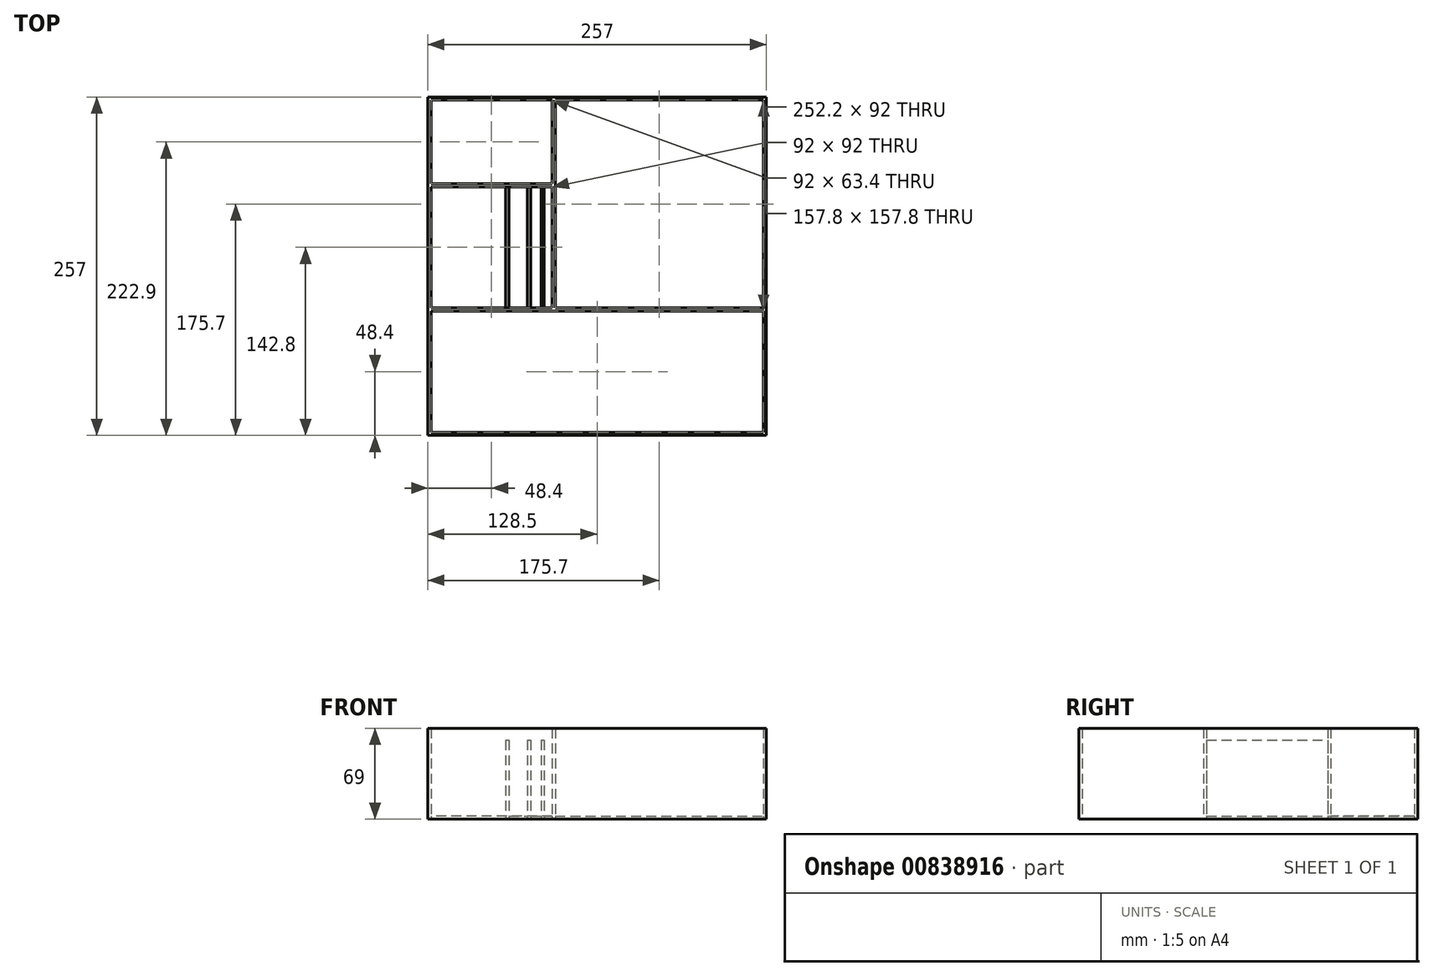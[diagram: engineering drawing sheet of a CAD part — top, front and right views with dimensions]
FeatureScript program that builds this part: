
annotation { "Feature Type Name" : "Feature", "Feature Type Description" : "" }
export const myFeature = defineFeature(function(context is Context, id is Id, definition is map)
    precondition{}
    {
        {
            var Q0;
            Q0=qCreatedBy(makeId("Top.planeOp"),FACE);
            var sketch = newSketch(context, id + "F0", { "sketchPlane" : qUnion([Q0])});
            skLineSegment(sketch, "E0.bottom", {"start": v(128.5, 128.5) * mm, "end": v(-128.5, 128.5) * mm});
            skLineSegment(sketch, "E0.top", {"start": v(128.5, -128.5) * mm, "end": v(-128.5, -128.5) * mm});
            skLineSegment(sketch, "E0.left", {"start": v(128.5, 128.5) * mm, "end": v(128.5, -128.5) * mm});
            skLineSegment(sketch, "E0.right", {"start": v(-128.5, 128.5) * mm, "end": v(-128.5, -128.5) * mm});
            skPoint(sketch, "E0.middle", {"position": v(0, 0) * mm});
            skLineSegment(sketch, "E1.0", {"start": v(-126.1, 126.1) * mm, "end": v(-126.1, -126.1) * mm});
            skLineSegment(sketch, "E1.1", {"start": v(126.1, 126.1) * mm, "end": v(-126.1, 126.1) * mm});
            skLineSegment(sketch, "E1.2", {"start": v(126.1, 126.1) * mm, "end": v(126.1, -126.1) * mm});
            skLineSegment(sketch, "E1.3", {"start": v(126.1, -126.1) * mm, "end": v(-126.1, -126.1) * mm});
            skLineSegment(sketch, "E2.bottom", {"start": v(-126.1, -126.1) * mm, "end": v(126.1, -126.1) * mm});
            skLineSegment(sketch, "E2.top", {"start": v(-126.1, -34.1) * mm, "end": v(126.1, -34.1) * mm});
            skLineSegment(sketch, "E2.left", {"start": v(-126.1, -126.1) * mm, "end": v(-126.1, -34.1) * mm});
            skLineSegment(sketch, "E2.right", {"start": v(126.1, -126.1) * mm, "end": v(126.1, -34.1) * mm});
            skLineSegment(sketch, "E3.0", {"start": v(-126.1, -31.7) * mm, "end": v(126.1, -31.7) * mm});
            skLineSegment(sketch, "E4.bottom", {"start": v(-126.1, -31.7) * mm, "end": v(-34.1, -31.7) * mm});
            skLineSegment(sketch, "E4.top", {"start": v(-126.1, 60.3) * mm, "end": v(-34.1, 60.3) * mm});
            skLineSegment(sketch, "E4.left", {"start": v(-126.1, -31.7) * mm, "end": v(-126.1, 60.3) * mm});
            skLineSegment(sketch, "E4.right", {"start": v(-34.1, -31.7) * mm, "end": v(-34.1, 60.3) * mm});
            skLineSegment(sketch, "E5", {"start": v(-34.1, 60.3) * mm, "end": v(-34.1, 126.1) * mm});
            skLineSegment(sketch, "E6.0", {"start": v(-126.1, 62.7) * mm, "end": v(-34.1, 62.7) * mm});
            skLineSegment(sketch, "E7.0", {"start": v(-31.7, 60.3) * mm, "end": v(-31.7, 126.1) * mm});
            skLineSegment(sketch, "E7.1", {"start": v(-31.7, -31.7) * mm, "end": v(-31.7, 60.3) * mm});
            skLineSegment(sketch, "E8.0", {"start": v(-40.1, -31.7) * mm, "end": v(-40.1, 60.3) * mm});
            skLineSegment(sketch, "E9.0", {"start": v(-42.5, -31.7) * mm, "end": v(-42.5, 60.3) * mm});
            skLineSegment(sketch, "E10.0", {"start": v(-50.5, -31.7) * mm, "end": v(-50.5, 60.3) * mm});
            skLineSegment(sketch, "E11.0", {"start": v(-52.9, -31.7) * mm, "end": v(-52.9, 60.3) * mm});
            skLineSegment(sketch, "E12.0", {"start": v(-66.9, -31.7) * mm, "end": v(-66.9, 60.3) * mm});
            skLineSegment(sketch, "E13.0", {"start": v(-69.3, -31.7) * mm, "end": v(-69.3, 60.3) * mm});
            skSolve(sketch);
        }
        {
            var Q0;
            {var subQ3=sQuery(id+"F0.wireOp",EDGE,"E6.0");Q0=makeQuery(id+"F0.imprint","IMPRINT",FACE,{"disambiguationData":[TD([[makeQuery(id+"F0.imprint","IMPRINT",EDGE,{"derivedFrom":subQ3}),1.0]])]});}
            var Q1;
            {var subQ0=sQuery(id+"F0.wireOp",EDGE,"E4.left");Q1=makeQuery(id+"F0.imprint","IMPRINT",FACE,{"disambiguationData":[TD([[makeQuery(id+"F0.imprint","IMPRINT",EDGE,{"derivedFrom":subQ0}),-1.0]])]});}
            var Q2;
            {var subQ0=sQuery(id+"F0.wireOp",EDGE,"E11.0");Q2=makeQuery(id+"F0.imprint","IMPRINT",FACE,{"disambiguationData":[TD([[makeQuery(id+"F0.imprint","IMPRINT",EDGE,{"derivedFrom":subQ0}),1.0]])]});}
            var Q3;
            {var subQ0=sQuery(id+"F0.wireOp",EDGE,"E9.0");Q3=makeQuery(id+"F0.imprint","IMPRINT",FACE,{"disambiguationData":[TD([[makeQuery(id+"F0.imprint","IMPRINT",EDGE,{"derivedFrom":subQ0}),1.0]])]});}
            var Q4;
            {var subQ0=sQuery(id+"F0.wireOp",EDGE,"E4.right");Q4=makeQuery(id+"F0.imprint","IMPRINT",FACE,{"disambiguationData":[TD([[makeQuery(id+"F0.imprint","IMPRINT",EDGE,{"derivedFrom":subQ0}),1.0]])]});}
            var Q5;
            {var subQ5=sQuery(id+"F0.wireOp",EDGE,"E7.0");Q5=makeQuery(id+"F0.imprint","IMPRINT",FACE,{"disambiguationData":[TD([[makeQuery(id+"F0.imprint","IMPRINT",EDGE,{"derivedFrom":subQ5}),-1.0]])]});}
            var Q6;
            Q6=makeQuery(id+"F0.imprint","IMPRINT",FACE,{"disambiguationData":[TD([[makeQuery(id+"F0.imprint","IMPRINT",EDGE,{"derivedFrom":sQuery(id+"F0.wireOp",EDGE,"E2.bottom")}),1.0]])]});
            extrude(context, id + "F1", {"entities" : qUnion([Q0, Q1, Q2, Q3, Q4, Q5, Q6]), "depth" : 2.4 * mm, "offsetDistance" : 25 * mm});
        }
        {
            var Q0;
            Q0=makeQuery(id+"F0.imprint","IMPRINT",FACE,{"disambiguationData":[TD([[makeQuery(id+"F0.imprint","IMPRINT",EDGE,{"derivedFrom":sQuery(id+"F0.wireOp",EDGE,"E0.bottom")}),1.0]])]});
            var Q1;
            {var subQ11=sQuery(id+"F0.wireOp",EDGE,"E2.top");Q1=makeQuery(id+"F0.imprint","IMPRINT",FACE,{"disambiguationData":[TD([[makeQuery(id+"F0.imprint","IMPRINT",EDGE,{"derivedFrom":subQ11}),1.0]])]});}
            var Q2;
            {var subQ5=sQuery(id+"F0.wireOp",EDGE,"E6.0");Q2=makeQuery(id+"F0.imprint","IMPRINT",FACE,{"disambiguationData":[TD([[makeQuery(id+"F0.imprint","IMPRINT",EDGE,{"derivedFrom":subQ5}),-1.0]])]});}
            var Q3;
            {var subQ1=sQuery(id+"F0.wireOp",EDGE,"E4.right");Q3=makeQuery(id+"F0.imprint","IMPRINT",FACE,{"disambiguationData":[TD([[makeQuery(id+"F0.imprint","IMPRINT",EDGE,{"derivedFrom":subQ1}),-1.0]])]});}
            extrude(context, id + "F2", {"entities" : qUnion([Q0, Q1, Q2, Q3]), "depth" : 69 * mm, "offsetDistance" : 25 * mm});
        }
        {
            var Q0;
            {var subQ0=sQuery(id+"F0.wireOp",EDGE,"E12.0");Q0=makeQuery(id+"F0.imprint","IMPRINT",FACE,{"disambiguationData":[TD([[makeQuery(id+"F0.imprint","IMPRINT",EDGE,{"derivedFrom":subQ0}),1.0]])]});}
            var Q1;
            {var subQ0=sQuery(id+"F0.wireOp",EDGE,"E10.0");Q1=makeQuery(id+"F0.imprint","IMPRINT",FACE,{"disambiguationData":[TD([[makeQuery(id+"F0.imprint","IMPRINT",EDGE,{"derivedFrom":subQ0}),1.0]])]});}
            var Q2;
            {var subQ0=sQuery(id+"F0.wireOp",EDGE,"E8.0");Q2=makeQuery(id+"F0.imprint","IMPRINT",FACE,{"disambiguationData":[TD([[makeQuery(id+"F0.imprint","IMPRINT",EDGE,{"derivedFrom":subQ0}),1.0]])]});}
            extrude(context, id + "F3", {"entities" : qUnion([Q0, Q1, Q2]), "depth" : 60 * mm, "offsetDistance" : 25 * mm});
        }
    });
